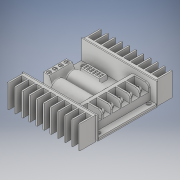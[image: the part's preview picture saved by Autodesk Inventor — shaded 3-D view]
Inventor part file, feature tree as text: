
AUTODESK INVENTOR PART (.ipt)
format: ipt  version: 2017 (Build 210142000, 142)  size: 432,640 bytes
history: native  units: in
note: dims shown in document units (in); Inventor stores cm internally (conversion verified against a paired STEP export)
features: other x9, mirror x2, fillet x1
ambient origin geometry x8: Origin, YZ Plane, XZ Plane, XY Plane, X Axis, Y Axis, Z Axis, Center Point
bodies: Solid1 (feature_tree), Solid2 (feature_tree), Solid3 (feature_tree), Solid4 (feature_tree), Solid5 (feature_tree), Solid6 (feature_tree), Solid7 (feature_tree), Solid8 (feature_tree), Solid9 (feature_tree), Solid10 (feature_tree), Solid11 (feature_tree), Solid12 (feature_tree)
feature tree (12):
  fillet  "Fillet5"  [1 undecoded]
  mirror  "Mirror5"
  other  "LPattern3"
  mirror  "Mirror6"
  other  "Cut-Extrude3[2]"
  other  "Boss-Extrude16[1]"
  other  "Boss-Extrude16[2]"
  other  "Boss-Extrude16[3]"
  other  "Boss-Extrude16[4]"
  other  "Boss-Extrude16[5]"
  other  "Boss-Extrude16[6]"
  other  "LPattern5"
note: 1 required parameter value undecoded (feature->parameter linkage not recoverable at this tier; creation-order binding heuristic only, values carry confidence <= 0.55)
